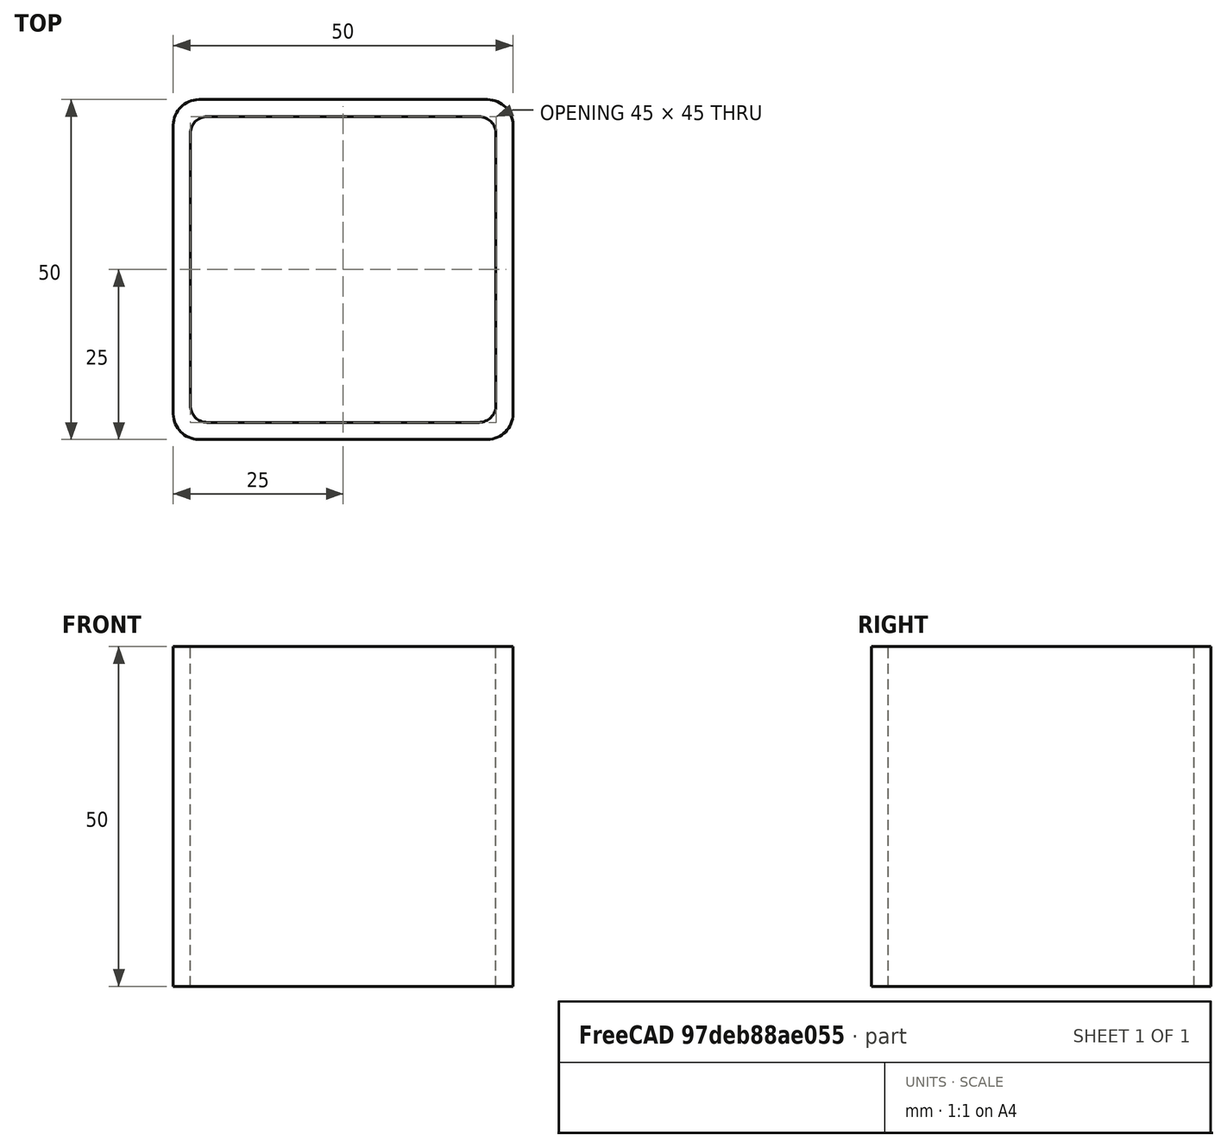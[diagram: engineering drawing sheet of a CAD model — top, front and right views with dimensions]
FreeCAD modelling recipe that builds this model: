
FCSTD DOCUMENT  (FreeCAD 0.15R4671 (Git))
Label: Square hollow section 50x50x2.5 EN10219 S235JRH
License: All rights reserved
LicenseURL: http://en.wikipedia.org/wiki/All_rights_reserved
objects: Sketcher::SketchObject×1, Part::Extrusion×1
note: 2 computed .brp shape members not serialized (recipe doc carries the construction recipe); baked Part::Feature solids carry a one-line shape summary decoded from their .brp

FEATURE [Sketcher::SketchObject] Sketch
  sketch-geometry (16):
    g0: LineSegment StartX=-20 StartY=22.5 StartZ=0 EndX=20 EndY=22.5 EndZ=0
    g1: LineSegment StartX=22.5 StartY=20 StartZ=0 EndX=22.5 EndY=-20 EndZ=0
    g2: LineSegment StartX=20 StartY=-22.5 StartZ=0 EndX=-20 EndY=-22.5 EndZ=0
    g3: LineSegment StartX=-22.5 StartY=-20 StartZ=0 EndX=-22.5 EndY=20 EndZ=0
    g4: LineSegment StartX=-21.25 StartY=25 StartZ=0 EndX=21.25 EndY=25 EndZ=0
    g5: LineSegment StartX=25 StartY=21.25 StartZ=0 EndX=25 EndY=-21.25 EndZ=0
    g6: LineSegment StartX=21.25 StartY=-25 StartZ=0 EndX=-21.25 EndY=-25 EndZ=0
    g7: LineSegment StartX=-25 StartY=-21.25 StartZ=0 EndX=-25 EndY=21.25 EndZ=0
    g8: ArcOfCircle CenterX=-20 CenterY=20 CenterZ=0 NormalX=0 NormalY=0 NormalZ=1 Radius=2.5 StartAngle=1.5708 EndAngle=3.14159
    g9: ArcOfCircle CenterX=20 CenterY=20 CenterZ=0 NormalX=0 NormalY=0 NormalZ=1 Radius=2.5 StartAngle=0 EndAngle=1.5708
    g10: ArcOfCircle CenterX=20 CenterY=-20 CenterZ=0 NormalX=0 NormalY=0 NormalZ=1 Radius=2.5 StartAngle=4.71239 EndAngle=6.28319
    g11: ArcOfCircle CenterX=-20 CenterY=-20 CenterZ=0 NormalX=0 NormalY=0 NormalZ=1 Radius=2.5 StartAngle=3.14159 EndAngle=4.71239
    g12: ArcOfCircle CenterX=21.25 CenterY=21.25 CenterZ=0 NormalX=0 NormalY=0 NormalZ=1 Radius=3.75 StartAngle=0 EndAngle=1.5708
    g13: ArcOfCircle CenterX=21.25 CenterY=-21.25 CenterZ=0 NormalX=0 NormalY=0 NormalZ=1 Radius=3.75 StartAngle=4.71239 EndAngle=6.28319
    g14: ArcOfCircle CenterX=-21.25 CenterY=-21.25 CenterZ=0 NormalX=0 NormalY=0 NormalZ=1 Radius=3.75 StartAngle=3.14159 EndAngle=4.71239
    g15: ArcOfCircle CenterX=-21.25 CenterY=21.25 CenterZ=0 NormalX=0 NormalY=0 NormalZ=1 Radius=3.75 StartAngle=1.5708 EndAngle=3.14159
  constraints (36):
    c: Horizontal(g2)
    c: Vertical(g3)
    c: Horizontal(g6)
    c: Vertical(g7)
    c: Tangent(g3,g8) = 1.5708
    c: Tangent(g0,g8) = 1.5708
    c: Tangent(g0,g9) = 1.5708
    c: Tangent(g1,g9) = 1.5708
    c: Tangent(g1,g10) = 1.5708
    c: Tangent(g2,g10) = 1.5708
    c: Tangent(g2,g11) = 1.5708
    c: Tangent(g3,g11) = 1.5708
    c: Tangent(g4,g12) = 1.5708
    c: Tangent(g5,g12) = 1.5708
    c: Tangent(g5,g13) = 1.5708
    c: Tangent(g6,g13) = 1.5708
    c: Tangent(g6,g14) = 1.5708
    c: Tangent(g7,g14) = 1.5708
    c: Tangent(g7,g15) = 1.5708
    c: Tangent(g4,g15) = 1.5708
    c: Equal(g9,g8)
    c: Equal(g9,g11)
    c: Equal(g9,g10)
    c: Equal(g12,g15)
    c: Equal(g12,g14)
    c: Equal(g12,g13)
    c: Symmetric(g4,g6,g-1)
    c: Symmetric(g7,g5,g-2)
    c: DistanceY(g4,g6) = -50
    c: DistanceX(g7,g5) = 50
    c: Symmetric(g3,g1,g-2)
    c: Symmetric(g0,g2,g-1)
    c: DistanceY(g0,g4) = 2.5
    c: DistanceX(g5,g1) = -2.5
    c: Radius(g9) = 2.5
    c: Radius(g12) = 3.75
FEATURE [Part::Extrusion] Extrude  label="Square hollow section 50x50x2.5 EN10219 S235JRH"
  Base = -> Sketch
  Dir = (0,0,50)
  Solid = true
